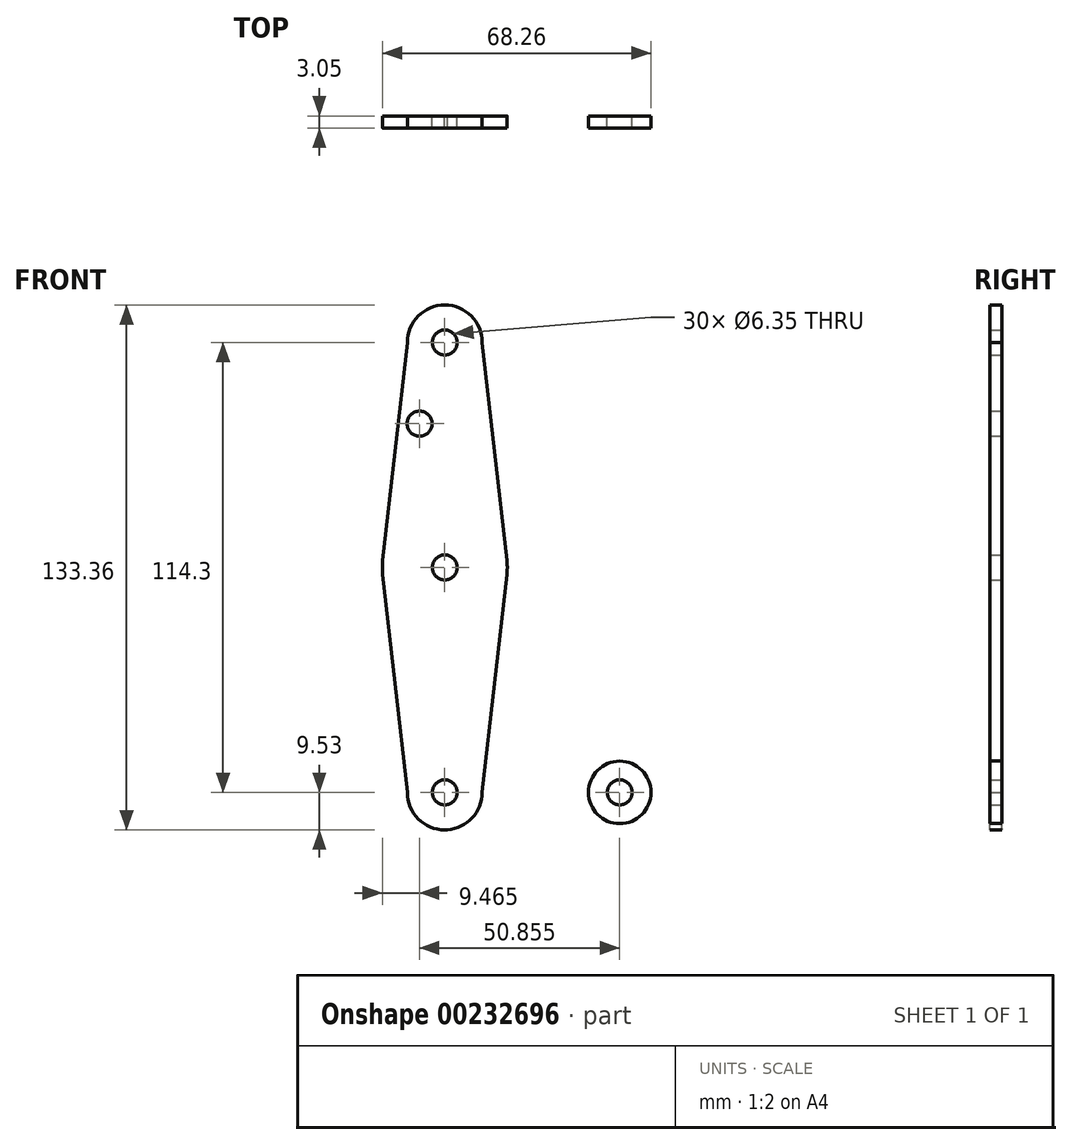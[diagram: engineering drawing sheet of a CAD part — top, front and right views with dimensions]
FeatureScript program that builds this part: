
annotation { "Feature Type Name" : "Feature", "Feature Type Description" : "" }
export const myFeature = defineFeature(function(context is Context, id is Id, definition is map)
    precondition{}
    {
        {
            var Q0;
            Q0=qCreatedBy(makeId("Front.planeOp"),FACE);
            var sketch = newSketch(context, id + "F0", { "sketchPlane" : qUnion([Q0])});
            skLineSegment(sketch, "E0", {"start": v(0, 0) * mm, "end": v(0, 114.3) * mm, "construction": true});
            skCircle(sketch, "E1", {"center": v(0, 57.15) * mm, "radius": 15.88 * mm});
            skCircle(sketch, "E2", {"center": v(0, 114.3) * mm, "radius": 9.53 * mm});
            skCircle(sketch, "E3", {"center": v(0, 0) * mm, "radius": 9.53 * mm});
            skLineSegment(sketch, "E4", {"start": v(0, 0) * mm, "end": v(44.45, 0) * mm, "construction": true});
            skCircle(sketch, "E5", {"center": v(44.45, 0) * mm, "radius": 7.94 * mm});
            skLineSegment(sketch, "E6", {"start": v(-9.52, 114.3) * mm, "end": v(-15.77, 58.93) * mm});
            skLineSegment(sketch, "E7", {"start": v(9.52, 114.3) * mm, "end": v(15.77, 58.93) * mm});
            skLineSegment(sketch, "E8", {"start": v(-15.77, 55.37) * mm, "end": v(-15.77, 58.93) * mm});
            skLineSegment(sketch, "E9", {"start": v(19.05, 8.85) * mm, "end": v(44.73, 7.93) * mm});
            skLineSegment(sketch, "E10", {"start": v(0, -9.53) * mm, "end": v(44.73, -7.93) * mm});
            skCircle(sketch, "E11", {"center": v(0, 114.3) * mm, "radius": 3.18 * mm});
            skCircle(sketch, "E12", {"center": v(0, 57.15) * mm, "radius": 3.18 * mm});
            skCircle(sketch, "E13", {"center": v(-6.4, 93.68) * mm, "radius": 3.18 * mm});
            skCircle(sketch, "E14", {"center": v(44.45, 0) * mm, "radius": 3.18 * mm});
            skArc(sketch, "E15.filletArc", {"start": v(11.43, 17.62) * mm, "mid": v(13.34, 11.58) * mm, "end": v(19.05, 8.85) * mm});
            skCircle(sketch, "E16", {"center": v(0, 0) * mm, "radius": 3.18 * mm});
            skLineSegment(sketch, "E17", {"start": v(9.53, 0) * mm, "end": v(15.77, 55.37) * mm});
            skLineSegment(sketch, "E18", {"start": v(-15.77, 55.37) * mm, "end": v(-9.53, 0) * mm});
            skSolve(sketch);
        }
        {
            var Q0;
            {var subQ0=sQuery(id+"F0.wireOp",EDGE,"E1");var subQ1=sQuery(id+"F0.wireOp",EDGE,"E0");var subQ2=makeQuery(id+"F0.imprint","INTERSECT",VERTEX,{"disambiguationData":[OD(0.0)],"derivedFrom":[subQ1,subQ0]});Q0=makeQuery(id+"F0.imprint","IMPRINT",FACE,{"disambiguationData":[TD([[makeQuery(id+"F0.imprint","IMPRINT",EDGE,{"disambiguationData":[TD([[subQ2,-1.0]])],"derivedFrom":subQ1}),1.0]])]});}
            var Q1;
            {var subQ0=sQuery(id+"F0.wireOp",EDGE,"E1");var subQ1=sQuery(id+"F0.wireOp",EDGE,"E0");var subQ2=makeQuery(id+"F0.imprint","INTERSECT",VERTEX,{"disambiguationData":[OD(0.0)],"derivedFrom":[subQ1,subQ0]});Q1=makeQuery(id+"F0.imprint","IMPRINT",FACE,{"disambiguationData":[TD([[makeQuery(id+"F0.imprint","IMPRINT",EDGE,{"disambiguationData":[TD([[subQ2,-1.0]])],"derivedFrom":subQ1}),-1.0]])]});}
            var Q2;
            {var subQ0=sQuery(id+"F0.wireOp",EDGE,"E2");var subQ1=makeQuery(id+"F0.imprint","INTERSECT",VERTEX,{"derivedFrom":[subQ0,sQuery(id+"F0.wireOp",EDGE,"E6")]});Q2=makeQuery(id+"F0.imprint","IMPRINT",FACE,{"disambiguationData":[TD([[makeQuery(id+"F0.imprint","IMPRINT",EDGE,{"disambiguationData":[TD([[subQ1,1.0]])],"derivedFrom":subQ0}),1.0]])]});}
            var Q3;
            {var subQ5=sQuery(id+"F0.wireOp",EDGE,"E7");Q3=makeQuery(id+"F0.imprint","IMPRINT",FACE,{"disambiguationData":[TD([[makeQuery(id+"F0.imprint","IMPRINT",EDGE,{"derivedFrom":subQ5}),-1.0]])]});}
            var Q4;
            {var subQ5=sQuery(id+"F0.wireOp",EDGE,"E6");Q4=makeQuery(id+"F0.imprint","IMPRINT",FACE,{"disambiguationData":[TD([[makeQuery(id+"F0.imprint","IMPRINT",EDGE,{"derivedFrom":subQ5}),1.0]])]});}
            var Q5;
            {var subQ0=sQuery(id+"F0.wireOp",EDGE,"d7A37Q1M-8xRa-t4OD-zYPU-SdT7yDJBlweH");var subQ1=sQuery(id+"F0.wireOp",EDGE,"E1");var subQ3=makeQuery(id+"F0.imprint","INTERSECT",VERTEX,{"derivedFrom":[subQ1,subQ0]});Q5=makeQuery(id+"F0.imprint","IMPRINT",FACE,{"disambiguationData":[TD([[makeQuery(id+"F0.imprint","IMPRINT",EDGE,{"disambiguationData":[TD([[subQ3,-1.0]])],"derivedFrom":subQ1}),1.0]])]});}
            var Q6;
            {var subQ0=sQuery(id+"F0.wireOp",EDGE,"E8");Q6=makeQuery(id+"F0.imprint","IMPRINT",FACE,{"disambiguationData":[TD([[makeQuery(id+"F0.imprint","IMPRINT",EDGE,{"derivedFrom":subQ0}),-1.0]])]});}
            var Q7;
            {var subQ0=sQuery(id+"F0.wireOp",EDGE,"E8");Q7=makeQuery(id+"F0.imprint","IMPRINT",FACE,{"disambiguationData":[TD([[makeQuery(id+"F0.imprint","IMPRINT",EDGE,{"derivedFrom":subQ0}),1.0]])]});}
            var Q8;
            {var subQ0=sQuery(id+"F0.wireOp",EDGE,"E10");var subQ5=sQuery(id+"F0.wireOp",EDGE,"E3");var subQ6=makeQuery(id+"F0.imprint","INTERSECT",VERTEX,{"disambiguationData":[OD(1.0)],"derivedFrom":[subQ5,subQ0]});Q8=makeQuery(id+"F0.imprint","IMPRINT",FACE,{"disambiguationData":[TD([[makeQuery(id+"F0.imprint","IMPRINT",EDGE,{"disambiguationData":[TD([[subQ6,-1.0]])],"derivedFrom":subQ5}),-1.0]])]});}
            var Q9;
            {var subQ0=sQuery(id+"F0.wireOp",EDGE,"d7A37Q1M-8xRa-t4OD-zYPU-SdT7yDJBlweH");var subQ1=sQuery(id+"F0.wireOp",EDGE,"E1");var subQ2=makeQuery(id+"F0.imprint","INTERSECT",VERTEX,{"derivedFrom":[subQ1,subQ0]});Q9=makeQuery(id+"F0.imprint","IMPRINT",FACE,{"disambiguationData":[TD([[makeQuery(id+"F0.imprint","IMPRINT",EDGE,{"disambiguationData":[TD([[subQ2,1.0]])],"derivedFrom":subQ1}),-1.0]])]});}
            var Q10;
            {var subQ0=sQuery(id+"F0.wireOp",EDGE,"E9");var subQ1=sQuery(id+"F0.wireOp",EDGE,"E3");var subQ2=makeQuery(id+"F0.imprint","INTERSECT",VERTEX,{"derivedFrom":[subQ1,subQ0]});Q10=makeQuery(id+"F0.imprint","IMPRINT",FACE,{"disambiguationData":[TD([[makeQuery(id+"F0.imprint","IMPRINT",EDGE,{"disambiguationData":[TD([[subQ2,1.0]])],"derivedFrom":subQ1}),-1.0]])]});}
            var Q11;
            {var subQ0=sQuery(id+"F0.wireOp",EDGE,"E5");var subQ1=makeQuery(id+"F0.imprint","INTERSECT",VERTEX,{"derivedFrom":[subQ0,sQuery(id+"F0.wireOp",EDGE,"E9")]});Q11=makeQuery(id+"F0.imprint","IMPRINT",FACE,{"disambiguationData":[TD([[makeQuery(id+"F0.imprint","IMPRINT",EDGE,{"disambiguationData":[TD([[subQ1,-1.0]])],"derivedFrom":subQ0}),1.0]])]});}
            var Q12;
            {var subQ3=sQuery(id+"F0.wireOp",EDGE,"E9");var subQ4=sQuery(id+"F0.wireOp",EDGE,"E3");var subQ6=makeQuery(id+"F0.imprint","INTERSECT",VERTEX,{"derivedFrom":[subQ4,subQ3]});Q12=makeQuery(id+"F0.imprint","IMPRINT",FACE,{"disambiguationData":[TD([[makeQuery(id+"F0.imprint","IMPRINT",EDGE,{"disambiguationData":[TD([[subQ6,1.0]])],"derivedFrom":subQ4}),1.0]])]});}
            var Q13;
            {var subQ3=sQuery(id+"F0.wireOp",EDGE,"E1");var subQ5=sQuery(id+"F0.wireOp",EDGE,"tvTyyS0d-IMrN-t3y4-krLc-BlKbqcRiExe7");var subQ7=makeQuery(id+"F0.imprint","INTERSECT",VERTEX,{"derivedFrom":[subQ3,subQ5]});Q13=makeQuery(id+"F0.imprint","IMPRINT",FACE,{"disambiguationData":[TD([[makeQuery(id+"F0.imprint","IMPRINT",EDGE,{"disambiguationData":[TD([[subQ7,-1.0]])],"derivedFrom":subQ3}),-1.0]])]});}
            var Q14;
            {var subQ0=sQuery(id+"F0.wireOp",EDGE,"d7A37Q1M-8xRa-t4OD-zYPU-SdT7yDJBlweH");var subQ1=sQuery(id+"F0.wireOp",EDGE,"E4");var subQ2=makeQuery(id+"F0.imprint","INTERSECT",VERTEX,{"derivedFrom":[subQ1,subQ0]});Q14=makeQuery(id+"F0.imprint","IMPRINT",FACE,{"disambiguationData":[TD([[makeQuery(id+"F0.imprint","IMPRINT",EDGE,{"disambiguationData":[TD([[subQ2,-1.0]])],"derivedFrom":subQ1}),1.0]])]});}
            var Q15;
            {var subQ1=sQuery(id+"F0.wireOp",EDGE,"E3");var subQ5=makeQuery(id+"F0.imprint","INTERSECT",VERTEX,{"derivedFrom":[subQ1,sQuery(id+"F0.wireOp",EDGE,"tvTyyS0d-IMrN-t3y4-krLc-BlKbqcRiExe7")]});Q15=makeQuery(id+"F0.imprint","IMPRINT",FACE,{"disambiguationData":[TD([[makeQuery(id+"F0.imprint","IMPRINT",EDGE,{"disambiguationData":[TD([[subQ5,-1.0]])],"derivedFrom":subQ1}),1.0]])]});}
            var Q16;
            {var subQ0=sQuery(id+"F0.wireOp",EDGE,"E10");var subQ1=sQuery(id+"F0.wireOp",EDGE,"E3");var subQ2=makeQuery(id+"F0.imprint","INTERSECT",VERTEX,{"disambiguationData":[OD(0.0)],"derivedFrom":[subQ1,subQ0]});Q16=makeQuery(id+"F0.imprint","IMPRINT",FACE,{"disambiguationData":[TD([[makeQuery(id+"F0.imprint","IMPRINT",EDGE,{"disambiguationData":[TD([[subQ2,-1.0]])],"derivedFrom":subQ1}),1.0]])]});}
            var Q17;
            {var subQ0=sQuery(id+"F0.wireOp",EDGE,"E9");var subQ1=sQuery(id+"F0.wireOp",EDGE,"E3");var subQ3=makeQuery(id+"F0.imprint","INTERSECT",VERTEX,{"derivedFrom":[subQ1,subQ0]});Q17=makeQuery(id+"F0.imprint","IMPRINT",FACE,{"disambiguationData":[TD([[makeQuery(id+"F0.imprint","IMPRINT",EDGE,{"disambiguationData":[TD([[subQ3,-1.0]])],"derivedFrom":subQ1}),1.0]])]});}
            extrude(context, id + "F1", {"entities" : qUnion([Q0, Q1, Q2, Q3, Q4, Q5, Q6, Q7, Q8, Q9, Q10, Q11, Q12, Q13, Q14, Q15, Q16, Q17]), "depth" : 3.05 * mm});
        }
    });
